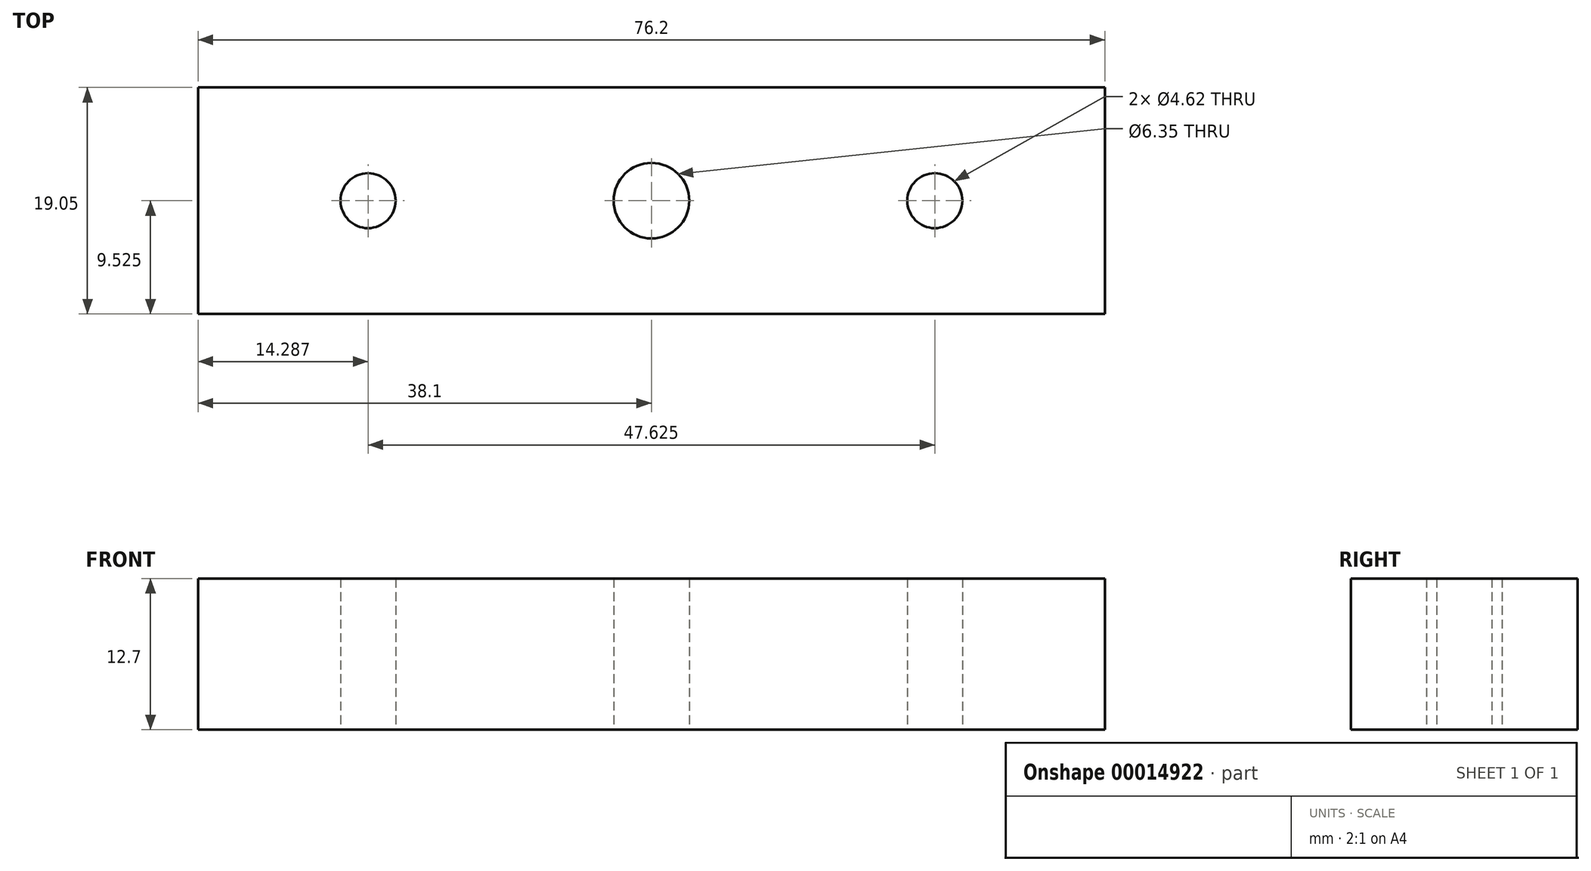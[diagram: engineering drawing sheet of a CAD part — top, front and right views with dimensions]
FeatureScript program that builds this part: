
annotation { "Feature Type Name" : "Feature", "Feature Type Description" : "" }
export const myFeature = defineFeature(function(context is Context, id is Id, definition is map)
    precondition{}
    {
        {
            var Q0;
            Q0=qCreatedBy(makeId("Top.planeOp"),FACE);
            var sketch = newSketch(context, id + "F0", { "sketchPlane" : qUnion([Q0])});
            skLineSegment(sketch, "E0.bottom", {"start": v(0, 0) * mm, "end": v(76.2, 0) * mm});
            skLineSegment(sketch, "E0.top", {"start": v(0, 19.05) * mm, "end": v(76.2, 19.05) * mm});
            skLineSegment(sketch, "E0.left", {"start": v(0, 0) * mm, "end": v(0, 19.05) * mm});
            skLineSegment(sketch, "E0.right", {"start": v(76.2, 0) * mm, "end": v(76.2, 19.05) * mm});
            skCircle(sketch, "E1", {"center": v(38.1, 9.53) * mm, "radius": 3.18 * mm});
            skCircle(sketch, "E2", {"center": v(61.91, 9.53) * mm, "radius": 2.31 * mm});
            skCircle(sketch, "E3", {"center": v(14.29, 9.53) * mm, "radius": 2.31 * mm});
            skSolve(sketch);
        }
        {
            var Q0;
            Q0=makeQuery(id+"F0.imprint","IMPRINT",FACE,{"disambiguationData":[TD([[makeQuery(id+"F0.imprint","IMPRINT",EDGE,{"derivedFrom":sQuery(id+"F0.wireOp",EDGE,"E0.bottom")}),1.0]])]});
            extrude(context, id + "F1", {"entities" : qUnion([Q0]), "depth" : 12.7 * mm});
        }
    });
